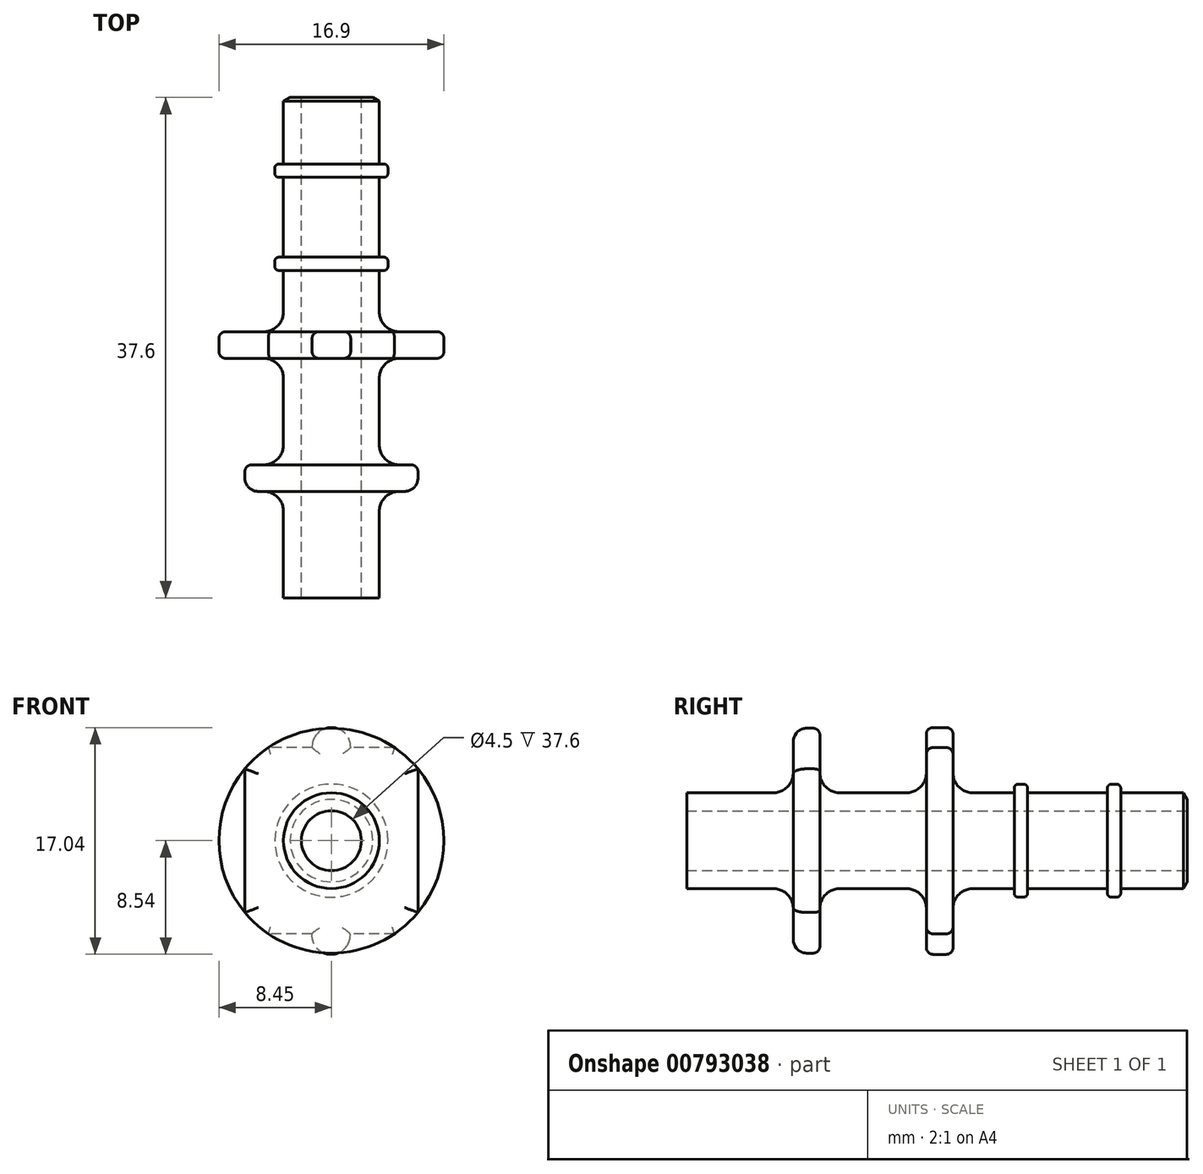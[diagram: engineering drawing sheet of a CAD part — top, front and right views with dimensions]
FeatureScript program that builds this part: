
annotation { "Feature Type Name" : "Feature", "Feature Type Description" : "" }
export const myFeature = defineFeature(function(context is Context, id is Id, definition is map)
    precondition{}
    {
        {
            var Q0;
            Q0=qCreatedBy(makeId("Front.planeOp"),FACE);
            var sketch = newSketch(context, id + "F0", { "sketchPlane" : qUnion([Q0])});
            skCircle(sketch, "E0", {"center": v(0, 0) * mm, "radius": 3.6 * mm});
            skCircle(sketch, "E1", {"center": v(0, 0) * mm, "radius": 2.25 * mm});
            skSolve(sketch);
        }
        {
            var Q0;
            Q0=makeQuery(id+"F0.imprint","IMPRINT",FACE,{"disambiguationData":[TD([[makeQuery(id+"F0.imprint","IMPRINT",EDGE,{"derivedFrom":sQuery(id+"F0.wireOp",EDGE,"E0")}),1.0]])]});
            extrude(context, id + "F1", {"entities" : qUnion([Q0]), "depth" : 37.6 * mm, "offsetDistance" : 25 * mm});
        }
        {
            var Q0;
            Q0=qCreatedBy(makeId("Front.planeOp"),FACE);
            cPlane(context, id + "F2", {"entities" : qUnion([Q0]), "cplaneType" : CPlaneType.OFFSET, "offset" : 6 * mm, "width" : 150 * mm, "height" : 150 * mm});
        }
        {
            var Q0;
            Q0=qCreatedBy(makeId("Front.planeOp"),FACE);
            cPlane(context, id + "F3", {"entities" : qUnion([Q0]), "cplaneType" : CPlaneType.OFFSET, "offset" : 13 * mm, "width" : 150 * mm, "height" : 150 * mm});
        }
        {
            var Q0;
            Q0=qCreatedBy(makeId("Front.planeOp"),FACE);
            cPlane(context, id + "F4", {"entities" : qUnion([Q0]), "cplaneType" : CPlaneType.OFFSET, "offset" : 17.6 * mm, "width" : 150 * mm, "height" : 150 * mm});
        }
        {
            var Q0;
            Q0=qCreatedBy(makeId("Front.planeOp"),FACE);
            cPlane(context, id + "F5", {"entities" : qUnion([Q0]), "cplaneType" : CPlaneType.OFFSET, "offset" : 27.6 * mm, "width" : 150 * mm, "height" : 150 * mm});
        }
        {
            var Q0;
            Q0=qCreatedBy(id+"F2.planeOp",FACE);
            var sketch = newSketch(context, id + "F6", { "sketchPlane" : qUnion([Q0])});
            skCircle(sketch, "E2", {"center": v(0, 0) * mm, "radius": 4.25 * mm});
            skCircle(sketch, "E3", {"center": v(0, 0) * mm, "radius": 2.25 * mm});
            skSolve(sketch);
        }
        {
            var Q0;
            Q0=makeQuery(id+"F6.imprint","IMPRINT",FACE,{"disambiguationData":[TD([[makeQuery(id+"F6.imprint","IMPRINT",EDGE,{"derivedFrom":sQuery(id+"F6.wireOp",EDGE,"E2")}),1.0]])]});
            extrude(context, id + "F7", {"entities" : qUnion([Q0]), "operationType" : NewBodyOperationType.ADD, "oppositeDirection" : true, "depth" : 1 * mm, "offsetDistance" : 25 * mm});
        }
        {
            var Q0;
            Q0=qCreatedBy(id+"F3.planeOp",FACE);
            var sketch = newSketch(context, id + "F8", { "sketchPlane" : qUnion([Q0])});
            skCircle(sketch, "E4", {"center": v(0, 0) * mm, "radius": 4.25 * mm});
            skCircle(sketch, "E5", {"center": v(0, 0) * mm, "radius": 2.25 * mm});
            skSolve(sketch);
        }
        {
            var Q0;
            Q0=makeQuery(id+"F8.imprint","IMPRINT",FACE,{"disambiguationData":[TD([[makeQuery(id+"F8.imprint","IMPRINT",EDGE,{"derivedFrom":sQuery(id+"F8.wireOp",EDGE,"E4")}),1.0]])]});
            extrude(context, id + "F9", {"entities" : qUnion([Q0]), "operationType" : NewBodyOperationType.ADD, "oppositeDirection" : true, "depth" : 1 * mm, "offsetDistance" : 25 * mm});
        }
        {
            var Q0;
            Q0=qCreatedBy(id+"F4.planeOp",FACE);
            var sketch = newSketch(context, id + "F10", { "sketchPlane" : qUnion([Q0])});
            skArc(sketch, "E6", {"start": v(1.45, 7) * mm, "mid": v(0, 8.5) * mm, "end": v(-1.45, 7) * mm});
            skArc(sketch, "E7", {"start": v(-1.48, -7) * mm, "mid": v(-0.03, -8.54) * mm, "end": v(1.42, -7) * mm});
            skArc(sketch, "E8", {"start": v(4.73, -7) * mm, "mid": v(8.45, 0) * mm, "end": v(4.73, 7) * mm});
            skArc(sketch, "E9", {"start": v(-4.73, 7) * mm, "mid": v(-8.45, 0) * mm, "end": v(-4.73, -7) * mm});
            skLineSegment(sketch, "E10", {"start": v(4.73, 7) * mm, "end": v(1.45, 7) * mm});
            skLineSegment(sketch, "E11", {"start": v(-1.45, 7) * mm, "end": v(-4.73, 7) * mm});
            skLineSegment(sketch, "E12", {"start": v(4.73, -7) * mm, "end": v(1.42, -7) * mm});
            skLineSegment(sketch, "E13", {"start": v(-1.48, -7) * mm, "end": v(-4.73, -7) * mm});
            skCircle(sketch, "E14", {"center": v(0, 0) * mm, "radius": 2.25 * mm});
            skSolve(sketch);
        }
        {
            var Q0;
            Q0=makeQuery(id+"F10.imprint","IMPRINT",FACE,{"disambiguationData":[TD([[makeQuery(id+"F10.imprint","IMPRINT",EDGE,{"derivedFrom":sQuery(id+"F10.wireOp",EDGE,"E6")}),1.0]])]});
            extrude(context, id + "F11", {"entities" : qUnion([Q0]), "operationType" : NewBodyOperationType.ADD, "depth" : 2 * mm, "offsetDistance" : 25 * mm});
        }
        {
            var Q0;
            Q0=qCreatedBy(id+"F5.planeOp",FACE);
            var sketch = newSketch(context, id + "F12", { "sketchPlane" : qUnion([Q0])});
            skLineSegment(sketch, "E15", {"start": v(6.5, 5.4) * mm, "end": v(-6.5, 5.4) * mm});
            skLineSegment(sketch, "E16", {"start": v(6.5, 5.4) * mm, "end": v(6.5, -5.4) * mm});
            skLineSegment(sketch, "E17", {"start": v(6.5, -5.4) * mm, "end": v(-6.5, -5.4) * mm});
            skLineSegment(sketch, "E18", {"start": v(-6.5, -5.4) * mm, "end": v(-6.5, 5.4) * mm});
            skArc(sketch, "E19", {"start": v(6.5, 5.4) * mm, "mid": v(0, 8.45) * mm, "end": v(-6.5, 5.4) * mm});
            skArc(sketch, "E20", {"start": v(-6.5, -5.4) * mm, "mid": v(0, -8.45) * mm, "end": v(6.5, -5.4) * mm});
            skCircle(sketch, "E21", {"center": v(0, 0) * mm, "radius": 2.25 * mm});
            skSolve(sketch);
        }
        {
            var Q0;
            Q0=makeQuery(id+"F12.imprint","IMPRINT",FACE,{"disambiguationData":[TD([[makeQuery(id+"F12.imprint","IMPRINT",EDGE,{"derivedFrom":sQuery(id+"F12.wireOp",EDGE,"E15")}),1.0]])]});
            var Q1;
            Q1=makeQuery(id+"F12.imprint","IMPRINT",FACE,{"disambiguationData":[TD([[makeQuery(id+"F12.imprint","IMPRINT",EDGE,{"derivedFrom":sQuery(id+"F12.wireOp",EDGE,"E17")}),1.0]])]});
            var Q2;
            Q2=makeQuery(id+"F12.imprint","IMPRINT",FACE,{"disambiguationData":[TD([[makeQuery(id+"F12.imprint","IMPRINT",EDGE,{"derivedFrom":sQuery(id+"F12.wireOp",EDGE,"E15")}),-1.0]])]});
            extrude(context, id + "F13", {"entities" : qUnion([Q0, Q1, Q2]), "operationType" : NewBodyOperationType.ADD, "depth" : 2 * mm, "offsetDistance" : 25 * mm});
        }
        {
            var Q0;
            Q0=makeQuery(id+"F1.opExtrude","CAP_EDGE",EDGE,{"disambiguationData":[OSD([sQuery(id+"F0.wireOp",EDGE,"E0")])],"isStart":true});
            chamfer(context, id + "F14", {"entities" : qUnion([Q0]), "chamferType" : ChamferType.OFFSET_ANGLE, "width" : 0.5 * mm, "oppositeDirection" : true, "angle" : 30 * degree, "tangentPropagation" : true});
        }
        {
            var Q0;
            {var subQ0=sQuery(id+"F0.wireOp",EDGE,"E0");var subQ1=makeQuery(id+"F1.opExtrude","CAP_FACE",FACE,{"disambiguationData":[OSD([subQ0,sQuery(id+"F0.wireOp",EDGE,"E1")])],"isStart":false});Q0=makeQuery(id+"F11.boolean.opBoolean","INTERSECT",EDGE,{"derivedFrom":[makeQuery(id+"F9.boolean.opBoolean","SPLIT",FACE,{"disambiguationData":[TD([subQ1])],"derivedFrom":makeQuery(id+"F7.boolean.opBoolean","SPLIT",FACE,{"disambiguationData":[TD([subQ1])],"derivedFrom":makeQuery(id+"F1.opExtrude","SWEPT_FACE",FACE,{"disambiguationData":[OSD([subQ0])]})})}),makeQuery(id+"F11.opExtrude","CAP_FACE",FACE,{"disambiguationData":[OSD([sQuery(id+"F10.wireOp",EDGE,"E6"),sQuery(id+"F10.wireOp",EDGE,"E7"),sQuery(id+"F10.wireOp",EDGE,"E8"),sQuery(id+"F10.wireOp",EDGE,"E9"),sQuery(id+"F10.wireOp",EDGE,"E10"),sQuery(id+"F10.wireOp",EDGE,"E11"),sQuery(id+"F10.wireOp",EDGE,"E12"),sQuery(id+"F10.wireOp",EDGE,"E13"),sQuery(id+"F10.wireOp",EDGE,"E14")])],"isStart":false})]});}
            fillet(context, id + "F15", {"entities" : qUnion([Q0]), "radius" : 1.5 * mm, "tangentPropagation" : true, "allowEdgeOverflow" : false});
        }
        {
            var Q0;
            {var subQ0=sQuery(id+"F0.wireOp",EDGE,"E0");var subQ1=makeQuery(id+"F1.opExtrude","CAP_FACE",FACE,{"disambiguationData":[OSD([subQ0,sQuery(id+"F0.wireOp",EDGE,"E1")])],"isStart":false});Q0=makeQuery(id+"F11.boolean.opBoolean","INTERSECT",EDGE,{"derivedFrom":[makeQuery(id+"F9.boolean.opBoolean","SPLIT",FACE,{"disambiguationData":[TD([subQ1])],"derivedFrom":makeQuery(id+"F7.boolean.opBoolean","SPLIT",FACE,{"disambiguationData":[TD([subQ1])],"derivedFrom":makeQuery(id+"F1.opExtrude","SWEPT_FACE",FACE,{"disambiguationData":[OSD([subQ0])]})})}),makeQuery(id+"F11.opExtrude","CAP_FACE",FACE,{"disambiguationData":[OSD([sQuery(id+"F10.wireOp",EDGE,"E6"),sQuery(id+"F10.wireOp",EDGE,"E7"),sQuery(id+"F10.wireOp",EDGE,"E8"),sQuery(id+"F10.wireOp",EDGE,"E9"),sQuery(id+"F10.wireOp",EDGE,"E10"),sQuery(id+"F10.wireOp",EDGE,"E11"),sQuery(id+"F10.wireOp",EDGE,"E12"),sQuery(id+"F10.wireOp",EDGE,"E13"),sQuery(id+"F10.wireOp",EDGE,"E14")])],"isStart":true})]});}
            fillet(context, id + "F16", {"entities" : qUnion([Q0]), "radius" : 1.5 * mm, "tangentPropagation" : true, "allowEdgeOverflow" : false});
        }
        {
            var Q0;
            {var subQ0=sQuery(id+"F0.wireOp",EDGE,"E0");var subQ1=makeQuery(id+"F1.opExtrude","CAP_FACE",FACE,{"disambiguationData":[OSD([subQ0,sQuery(id+"F0.wireOp",EDGE,"E1")])],"isStart":false});Q0=makeQuery(id+"F13.boolean.opBoolean","INTERSECT",EDGE,{"derivedFrom":[makeQuery(id+"F11.boolean.opBoolean","SPLIT",FACE,{"disambiguationData":[TD([subQ1])],"derivedFrom":makeQuery(id+"F9.boolean.opBoolean","SPLIT",FACE,{"disambiguationData":[TD([subQ1])],"derivedFrom":makeQuery(id+"F7.boolean.opBoolean","SPLIT",FACE,{"disambiguationData":[TD([subQ1])],"derivedFrom":makeQuery(id+"F1.opExtrude","SWEPT_FACE",FACE,{"disambiguationData":[OSD([subQ0])]})})})}),makeQuery(id+"F13.opExtrude","CAP_FACE",FACE,{"disambiguationData":[OSD([sQuery(id+"F12.wireOp",EDGE,"E16"),sQuery(id+"F12.wireOp",EDGE,"E18"),sQuery(id+"F12.wireOp",EDGE,"E19"),sQuery(id+"F12.wireOp",EDGE,"E20"),sQuery(id+"F12.wireOp",EDGE,"E21")])],"isStart":true})]});}
            var Q1;
            {var subQ0=sQuery(id+"F0.wireOp",EDGE,"E0");var subQ1=makeQuery(id+"F1.opExtrude","CAP_FACE",FACE,{"disambiguationData":[OSD([subQ0,sQuery(id+"F0.wireOp",EDGE,"E1")])],"isStart":false});Q1=makeQuery(id+"F13.boolean.opBoolean","INTERSECT",EDGE,{"derivedFrom":[makeQuery(id+"F11.boolean.opBoolean","SPLIT",FACE,{"disambiguationData":[TD([subQ1])],"derivedFrom":makeQuery(id+"F9.boolean.opBoolean","SPLIT",FACE,{"disambiguationData":[TD([subQ1])],"derivedFrom":makeQuery(id+"F7.boolean.opBoolean","SPLIT",FACE,{"disambiguationData":[TD([subQ1])],"derivedFrom":makeQuery(id+"F1.opExtrude","SWEPT_FACE",FACE,{"disambiguationData":[OSD([subQ0])]})})})}),makeQuery(id+"F13.opExtrude","CAP_FACE",FACE,{"disambiguationData":[OSD([sQuery(id+"F12.wireOp",EDGE,"E16"),sQuery(id+"F12.wireOp",EDGE,"E18"),sQuery(id+"F12.wireOp",EDGE,"E19"),sQuery(id+"F12.wireOp",EDGE,"E20"),sQuery(id+"F12.wireOp",EDGE,"E21")])],"isStart":false})]});}
            fillet(context, id + "F17", {"entities" : qUnion([Q0, Q1]), "radius" : 1.5 * mm, "tangentPropagation" : true, "allowEdgeOverflow" : false});
        }
        {
            var Q0;
            Q0=makeQuery(id+"F9.opExtrude","CAP_EDGE",EDGE,{"disambiguationData":[OSD([sQuery(id+"F8.wireOp",EDGE,"E4")])],"isStart":false});
            var Q1;
            Q1=makeQuery(id+"F9.opExtrude","CAP_EDGE",EDGE,{"disambiguationData":[OSD([sQuery(id+"F8.wireOp",EDGE,"E4")])],"isStart":true});
            fillet(context, id + "F18", {"entities" : qUnion([Q0, Q1]), "radius" : 0.3 * mm, "tangentPropagation" : true, "allowEdgeOverflow" : false});
        }
        {
            var Q0;
            Q0=makeQuery(id+"F13.opExtrude","CAP_EDGE",EDGE,{"disambiguationData":[OSD([sQuery(id+"F12.wireOp",EDGE,"E19")])],"isStart":true});
            var Q1;
            Q1=makeQuery(id+"F13.opExtrude","CAP_EDGE",EDGE,{"disambiguationData":[OSD([sQuery(id+"F12.wireOp",EDGE,"E18")])],"isStart":true});
            var Q2;
            Q2=makeQuery(id+"F13.opExtrude","CAP_EDGE",EDGE,{"disambiguationData":[OSD([sQuery(id+"F12.wireOp",EDGE,"E20")])],"isStart":true});
            var Q3;
            Q3=makeQuery(id+"F13.opExtrude","CAP_EDGE",EDGE,{"disambiguationData":[OSD([sQuery(id+"F12.wireOp",EDGE,"E16")])],"isStart":true});
            fillet(context, id + "F19", {"entities" : qUnion([Q0, Q1, Q2, Q3]), "radius" : 0.5 * mm, "tangentPropagation" : true, "allowEdgeOverflow" : false});
        }
        {
            var Q0;
            Q0=makeQuery(id+"F13.opExtrude","CAP_EDGE",EDGE,{"disambiguationData":[OSD([sQuery(id+"F12.wireOp",EDGE,"E18")])],"isStart":false});
            var Q1;
            Q1=makeQuery(id+"F13.opExtrude","CAP_EDGE",EDGE,{"disambiguationData":[OSD([sQuery(id+"F12.wireOp",EDGE,"E19")])],"isStart":false});
            var Q2;
            Q2=makeQuery(id+"F13.opExtrude","CAP_EDGE",EDGE,{"disambiguationData":[OSD([sQuery(id+"F12.wireOp",EDGE,"E16")])],"isStart":false});
            var Q3;
            Q3=makeQuery(id+"F13.opExtrude","CAP_EDGE",EDGE,{"disambiguationData":[OSD([sQuery(id+"F12.wireOp",EDGE,"E20")])],"isStart":false});
            fillet(context, id + "F20", {"entities" : qUnion([Q0, Q1, Q2, Q3]), "radius" : 1 * mm, "tangentPropagation" : true, "allowEdgeOverflow" : false});
        }
        {
            var Q0;
            Q0=makeQuery(id+"F11.opExtrude","CAP_EDGE",EDGE,{"disambiguationData":[OSD([sQuery(id+"F10.wireOp",EDGE,"E9")])],"isStart":false});
            var Q1;
            Q1=makeQuery(id+"F11.opExtrude","CAP_EDGE",EDGE,{"disambiguationData":[OSD([sQuery(id+"F10.wireOp",EDGE,"E11")])],"isStart":false});
            var Q2;
            Q2=makeQuery(id+"F11.opExtrude","CAP_EDGE",EDGE,{"disambiguationData":[OSD([sQuery(id+"F10.wireOp",EDGE,"E6")])],"isStart":false});
            var Q3;
            Q3=makeQuery(id+"F11.opExtrude","CAP_EDGE",EDGE,{"disambiguationData":[OSD([sQuery(id+"F10.wireOp",EDGE,"E10")])],"isStart":false});
            var Q4;
            Q4=makeQuery(id+"F11.opExtrude","CAP_EDGE",EDGE,{"disambiguationData":[OSD([sQuery(id+"F10.wireOp",EDGE,"E8")])],"isStart":false});
            var Q5;
            Q5=makeQuery(id+"F11.opExtrude","CAP_EDGE",EDGE,{"disambiguationData":[OSD([sQuery(id+"F10.wireOp",EDGE,"E12")])],"isStart":false});
            var Q6;
            Q6=makeQuery(id+"F11.opExtrude","CAP_EDGE",EDGE,{"disambiguationData":[OSD([sQuery(id+"F10.wireOp",EDGE,"E7")])],"isStart":false});
            var Q7;
            Q7=makeQuery(id+"F11.opExtrude","CAP_EDGE",EDGE,{"disambiguationData":[OSD([sQuery(id+"F10.wireOp",EDGE,"E13")])],"isStart":false});
            var Q8;
            Q8=makeQuery(id+"F11.opExtrude","CAP_EDGE",EDGE,{"disambiguationData":[OSD([sQuery(id+"F10.wireOp",EDGE,"E13")])],"isStart":true});
            var Q9;
            Q9=makeQuery(id+"F11.opExtrude","CAP_EDGE",EDGE,{"disambiguationData":[OSD([sQuery(id+"F10.wireOp",EDGE,"E7")])],"isStart":true});
            var Q10;
            Q10=makeQuery(id+"F11.opExtrude","CAP_EDGE",EDGE,{"disambiguationData":[OSD([sQuery(id+"F10.wireOp",EDGE,"E12")])],"isStart":true});
            var Q11;
            Q11=makeQuery(id+"F11.opExtrude","CAP_EDGE",EDGE,{"disambiguationData":[OSD([sQuery(id+"F10.wireOp",EDGE,"E8")])],"isStart":true});
            var Q12;
            Q12=makeQuery(id+"F11.opExtrude","CAP_EDGE",EDGE,{"disambiguationData":[OSD([sQuery(id+"F10.wireOp",EDGE,"E10")])],"isStart":true});
            var Q13;
            Q13=makeQuery(id+"F11.opExtrude","CAP_EDGE",EDGE,{"disambiguationData":[OSD([sQuery(id+"F10.wireOp",EDGE,"E6")])],"isStart":true});
            var Q14;
            Q14=makeQuery(id+"F11.opExtrude","CAP_EDGE",EDGE,{"disambiguationData":[OSD([sQuery(id+"F10.wireOp",EDGE,"E11")])],"isStart":true});
            var Q15;
            Q15=makeQuery(id+"F11.opExtrude","CAP_EDGE",EDGE,{"disambiguationData":[OSD([sQuery(id+"F10.wireOp",EDGE,"E9")])],"isStart":true});
            fillet(context, id + "F21", {"entities" : qUnion([Q0, Q1, Q2, Q3, Q4, Q5, Q6, Q7, Q8, Q9, Q10, Q11, Q12, Q13, Q14, Q15]), "radius" : 0.5 * mm, "tangentPropagation" : true, "allowEdgeOverflow" : false});
        }
        {
            var Q0;
            Q0=makeQuery(id+"F7.opExtrude","CAP_EDGE",EDGE,{"disambiguationData":[OSD([sQuery(id+"F6.wireOp",EDGE,"E2")])],"isStart":false});
            var Q1;
            Q1=makeQuery(id+"F7.opExtrude","CAP_EDGE",EDGE,{"disambiguationData":[OSD([sQuery(id+"F6.wireOp",EDGE,"E2")])],"isStart":true});
            fillet(context, id + "F22", {"entities" : qUnion([Q0, Q1]), "radius" : 0.3 * mm, "tangentPropagation" : true, "allowEdgeOverflow" : false});
        }
    });
